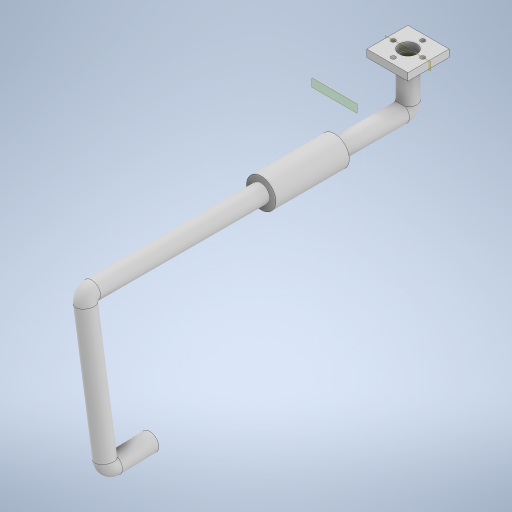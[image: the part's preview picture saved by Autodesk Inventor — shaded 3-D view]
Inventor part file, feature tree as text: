
AUTODESK INVENTOR PART (.ipt)
format: ipt  version: 2023 (Build 270158000, 158)  size: 358,912 bytes
history: native  units: mm
features: sketch x8, extrude x3, plane x2, sweep x1, chamfer x1
ambient origin geometry x8: Origin, YZ Plane, XZ Plane, XY Plane, X Axis, Y Axis, Z Axis, Center Point
bodies: Solid1 (feature_tree)
feature tree (15):
  extrude  "Extrusion1"  Depth=28.0mm
  extrude  "Extrusion2"  Depth=14.0mm
  plane  "Work Plane1"
  sketch  "Sketch3"  dims[d4=5.0mm d5=0.0mm d6=12.0mm]
  sketch  "3D Sketch1"
  sketch  "3D Sketch2"
  sweep  "Sweep1"
  chamfer  "Chamfer1"  Distance=40.0mm Angle=360.0deg
  sketch  "Sketch5"  dims[d8=10.0mm d9=40.0mm d11=360.0deg]
  plane  "Work Plane2"
  extrude  "Extrusion3"  [1 undecoded]
  sketch  "Sketch1"  dims[d0=28.0mm d1=28.0mm]
  sketch  "Sketch2"  dims[d2=14.0mm d3=14.0mm]
  sketch  "Sketch4"  dims[d7=3.0mm]
  sketch  "Sketch6"  dims[d13=5.0mm d14=0.0mm d15=-14.0mm d16=30.0mm d17=220.0mm d18=5.0mm d19=10.0mm d20=0.0mm d21=0.0mm d22=12.0mm d23=1.0mm d24=2.0mm d25=45.0deg d26=95.0mm d27=13.962634mm d28=5.0mm d29=30.0mm d30=90.0deg d31=5.0mm d32=90.0deg d33=-50.0mm d34=20.0mm d35=50.0mm d36=0.0mm]
note: 1 required parameter value undecoded (feature->parameter linkage not recoverable at this tier; creation-order binding heuristic only, values carry confidence <= 0.55)
